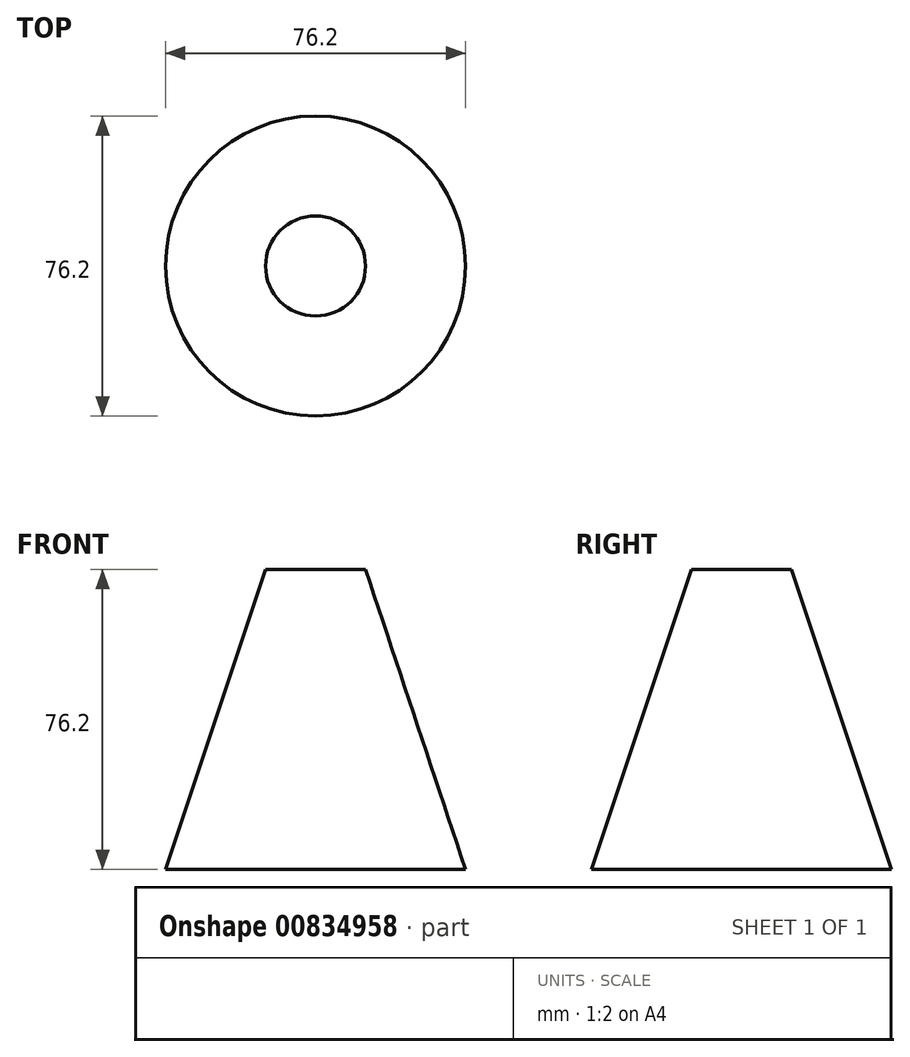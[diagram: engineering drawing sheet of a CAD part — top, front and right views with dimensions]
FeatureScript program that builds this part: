
annotation { "Feature Type Name" : "Feature", "Feature Type Description" : "" }
export const myFeature = defineFeature(function(context is Context, id is Id, definition is map)
    precondition{}
    {
        {
            var Q0;
            Q0=qCreatedBy(makeId("Top.planeOp"),FACE);
            var sketch = newSketch(context, id + "F0", { "sketchPlane" : qUnion([Q0])});
            skCircle(sketch, "E0", {"center": v(0, 0) * mm, "radius": 38.1 * mm});
            skCircle(sketch, "E1.0", {"center": v(0, 0) * mm, "radius": 40.64 * mm});
            skSolve(sketch);
        }
        {
            var Q0;
            Q0=qCreatedBy(makeId("Top.planeOp"),FACE);
            cPlane(context, id + "F1", {"entities" : qUnion([Q0]), "cplaneType" : CPlaneType.OFFSET, "offset" : 76.2 * mm, "width" : 152.4 * mm, "height" : 152.4 * mm});
        }
        {
            var Q0;
            Q0=qCreatedBy(id+"F1.planeOp",FACE);
            var sketch = newSketch(context, id + "F2", { "sketchPlane" : qUnion([Q0])});
            skCircle(sketch, "E2", {"center": v(0, 0) * mm, "radius": 12.7 * mm});
            skCircle(sketch, "E3.0", {"center": v(0, 0) * mm, "radius": 15.24 * mm});
            skSolve(sketch);
        }
        {
            var Q0;
            Q0=sQuery(id+"F2.wireOp",EDGE,"E2");
            var Q1;
            Q1=makeQuery(id+"F0.imprint","IMPRINT",FACE,{"disambiguationData":[TD([[makeQuery(id+"F0.imprint","IMPRINT",EDGE,{"derivedFrom":sQuery(id+"F0.wireOp",EDGE,"E0")}),1.0]])]});
            loft(context, id + "F3", {"bodyType" : ToolBodyType.SURFACE, "operationType" : NewBodyOperationType.ADD, "wireProfilesArray" : [{ "wireProfileEntities" : qUnion([Q0]) }, { "wireProfileEntities" : qUnion([Q1]) }]});
        }
    });
